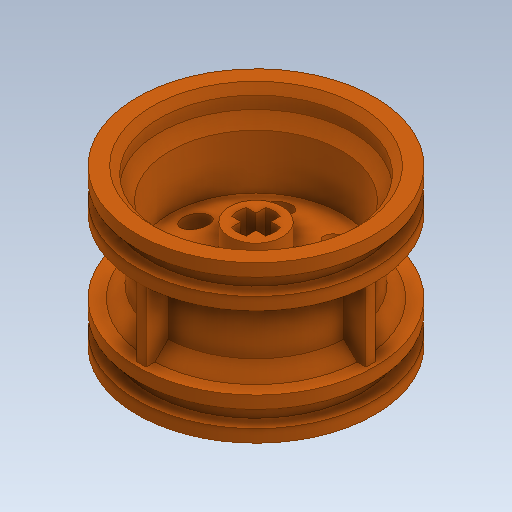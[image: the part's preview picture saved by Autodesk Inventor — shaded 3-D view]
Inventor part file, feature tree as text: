
AUTODESK INVENTOR PART (.ipt)
format: ipt  version: 2020 (Build 240168000, 168)  size: 545,280 bytes
history: native  units: mm
features: sketch x5, other x4, plane x1
ambient origin geometry x8: Origin, YZ Plane, XZ Plane, XY Plane, X Axis, Y Axis, Z Axis, Center Point
bodies: Body1 (feature_tree)
feature tree (10):
  other  "56145_Wheel.ipt"
  other  "Sólido1::56145_Wheel.ipt"
  other  "OperaçãoIdentificador1"
  sketch  "Sketch1"  dims[d0=10.0mm]
  sketch  "Sketch2"
  sketch  "Sketch3"
  sketch  "Sketch4"
  sketch  "Sketch5"
  plane  "Work Plane1"
  other  "Sólido1"
